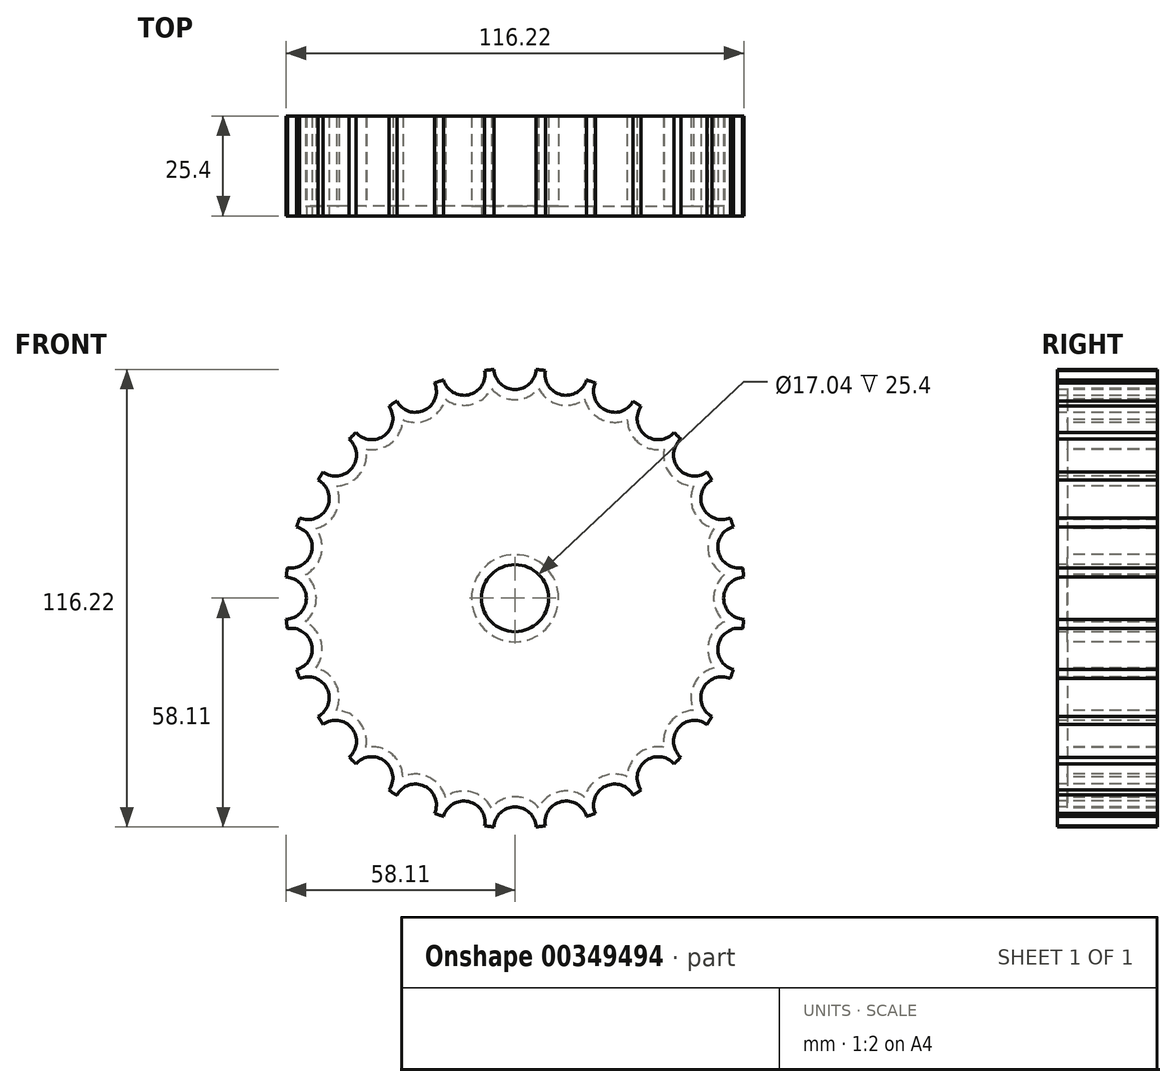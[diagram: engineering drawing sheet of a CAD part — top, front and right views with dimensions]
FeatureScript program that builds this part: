
annotation { "Feature Type Name" : "Feature", "Feature Type Description" : "" }
export const myFeature = defineFeature(function(context is Context, id is Id, definition is map)
    precondition{}
    {
        {
            var Q0;
            Q0=qCreatedBy(makeId("Front.planeOp"),FACE);
            var sketch = newSketch(context, id + "F0", { "sketchPlane" : qUnion([Q0])});
            skCircle(sketch, "E0", {"center": v(0, 0) * mm, "radius": 58.36 * mm});
            skSolve(sketch);
        }
        {
            var Q0;
            Q0=makeQuery(id+"F0.imprint","IMPRINT",FACE,{"disambiguationData":[TD([[makeQuery(id+"F0.imprint","IMPRINT",EDGE,{"derivedFrom":sQuery(id+"F0.wireOp",EDGE,"E0")}),1.0]])]});
            extrude(context, id + "F1", {"entities" : qUnion([Q0]), "depth" : 25.4 * mm});
        }
        {
            var Q0;
            Q0=makeQuery(id+"F1.opExtrude","CAP_FACE",FACE,{"disambiguationData":[OSD([sQuery(id+"F0.wireOp",EDGE,"E0")])],"isStart":false});
            var sketch = newSketch(context, id + "F2", { "sketchPlane" : qUnion([Q0])});
            skCircle(sketch, "E1", {"center": v(0, 58.36) * mm, "radius": 5.35 * mm});
            skSolve(sketch);
        }
        {
            var Q0;
            {var subQ0=sQuery(id+"F2.wireOp",EDGE,"E1");var subQ1=makeQuery(id+"F1.opExtrude","CAP_EDGE",EDGE,{"disambiguationData":[OSD([sQuery(id+"F0.wireOp",EDGE,"E0")])],"isStart":false});var subQ2=makeQuery(id+"F2.imprint","INTERSECT",VERTEX,{"disambiguationData":[OD(0.0)],"derivedFrom":[subQ1,subQ0]});Q0=makeQuery(id+"F2.imprint","IMPRINT",FACE,{"disambiguationData":[TD([[makeQuery(id+"F2.imprint","IMPRINT",EDGE,{"disambiguationData":[TD([[subQ2,-1.0]])],"derivedFrom":subQ0}),1.0]])]});}
            extrude(context, id + "F3", {"entities" : qUnion([Q0]), "operationType" : NewBodyOperationType.REMOVE, "endBound" : BoundingType.THROUGH_ALL, "oppositeDirection" : true, "depth" : 25.4 * mm});
        }
        {
            var Q0;
            Q0=makeQuery(id+"F3.boolean.opBoolean","COPY",FACE,{"derivedFrom":makeQuery(id+"F3.opExtrude","SWEPT_FACE",FACE,{"disambiguationData":[OSD([sQuery(id+"F2.wireOp",EDGE,"E1")])]})});
            var Q1;
            Q1=makeQuery(id+"F1.opExtrude","SWEPT_FACE",FACE,{"disambiguationData":[OSD([sQuery(id+"F0.wireOp",EDGE,"E0")])]});
            circularPattern(context, id + "F4", {"patternType" : PatternType.FACE, "faces" : qUnion([Q0]), "axis" : qUnion([Q1]), "angle" : 360 * degree, "instanceCount" : 28, "oppositeDirection" : true, "equalSpace" : true});
        }
        {
            var Q0;
            Q0=makeQuery(id+"F1.opExtrude","CAP_FACE",FACE,{"disambiguationData":[OSD([sQuery(id+"F0.wireOp",EDGE,"E0")])],"isStart":false});
            var sketch = newSketch(context, id + "F5", { "sketchPlane" : qUnion([Q0])});
            skCircle(sketch, "E2", {"center": v(0, 0) * mm, "radius": 8.52 * mm});
            skSolve(sketch);
        }
        {
            var Q0;
            Q0=makeQuery(id+"F5.imprint","IMPRINT",FACE,{"disambiguationData":[TD([[makeQuery(id+"F5.imprint","IMPRINT",EDGE,{"derivedFrom":sQuery(id+"F5.wireOp",EDGE,"E2")}),1.0]])]});
            extrude(context, id + "F6", {"entities" : qUnion([Q0]), "operationType" : NewBodyOperationType.REMOVE, "endBound" : BoundingType.THROUGH_ALL, "oppositeDirection" : true, "depth" : 25.4 * mm});
        }
        {
            var Q0;
            Q0=makeQuery(id+"F1.opExtrude","CAP_FACE",FACE,{"disambiguationData":[OSD([sQuery(id+"F0.wireOp",EDGE,"E0")])],"isStart":true});
            shell(context, id + "F7", {"entities" : qUnion([Q0]), "thickness" : 2.54 * mm});
        }
    });
